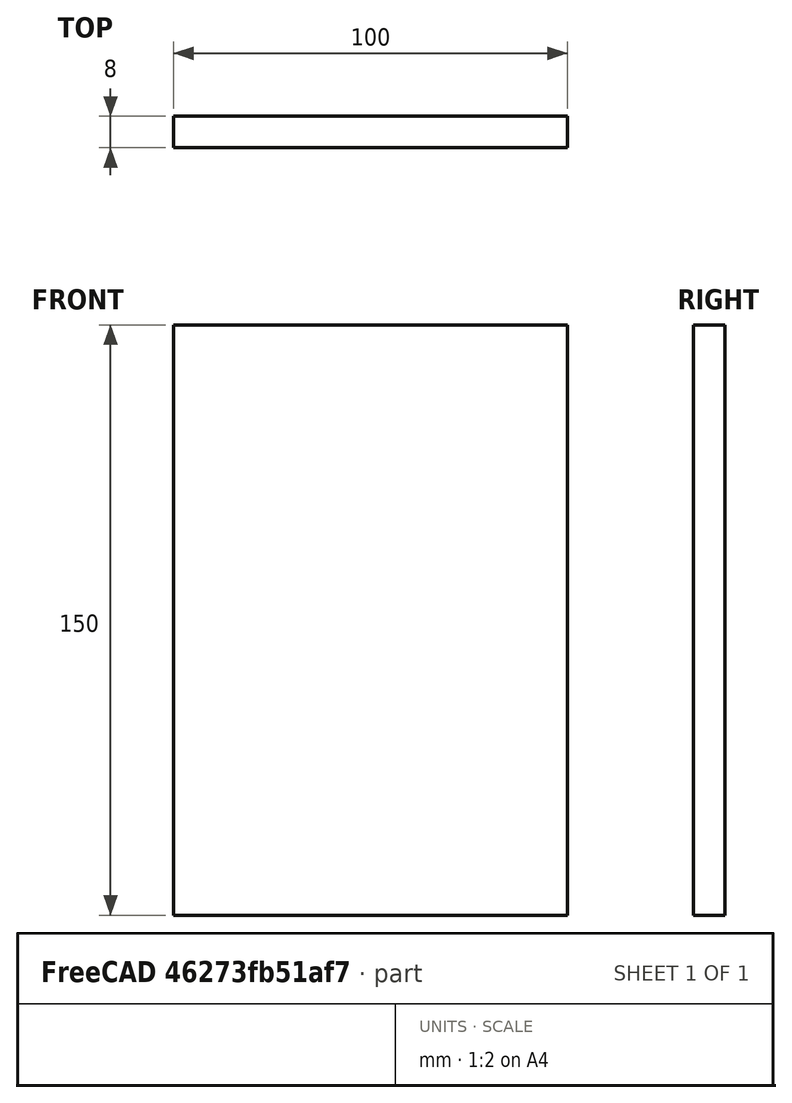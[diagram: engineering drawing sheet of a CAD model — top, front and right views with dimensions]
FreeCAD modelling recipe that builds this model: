
FCSTD DOCUMENT  (FreeCAD 0.15R4671 (Git))
Label: Hotwheel_CaraTrasera
License: All rights reserved
LicenseURL: http://es.wikipedia.org/wiki/Todos_los_derechos_reservados
objects: Sketcher::SketchObject×1, PartDesign::Pad×1
note: 3 computed .brp shape members not serialized (recipe doc carries the construction recipe); baked Part::Feature solids carry a one-line shape summary decoded from their .brp

FEATURE [Sketcher::SketchObject] Sketch
  Placement = pos=(0,0,0) rot=(-1,0,0;4.71239rad)
  sketch-geometry (4):
    g0: LineSegment StartX=-50 StartY=75 StartZ=0 EndX=50 EndY=75 EndZ=0
    g1: LineSegment StartX=50 StartY=75 StartZ=0 EndX=50 EndY=-75 EndZ=0
    g2: LineSegment StartX=50 StartY=-75 StartZ=0 EndX=-50 EndY=-75 EndZ=0
    g3: LineSegment StartX=-50 StartY=-75 StartZ=0 EndX=-50 EndY=75 EndZ=0
  constraints (12):
    c: Coincident(g0,g1)
    c: Coincident(g1,g2)
    c: Coincident(g2,g3)
    c: Coincident(g3,g0)
    c: Horizontal(g0)
    c: Horizontal(g2)
    c: Vertical(g1)
    c: Vertical(g3)
    c: DistanceX(g0,g0) = 100
    c: DistanceX(g-1,g0) = -50
    c: DistanceY(g1) = -150
    c: DistanceY(g-1,g0) = 75
FEATURE [PartDesign::Pad] Pad
  Length = 8
  Length2 = 100
  Placement = pos=(0,0,0) rot=(-1,0,0;4.71239rad)
  Sketch = -> Sketch
  Type = 0
